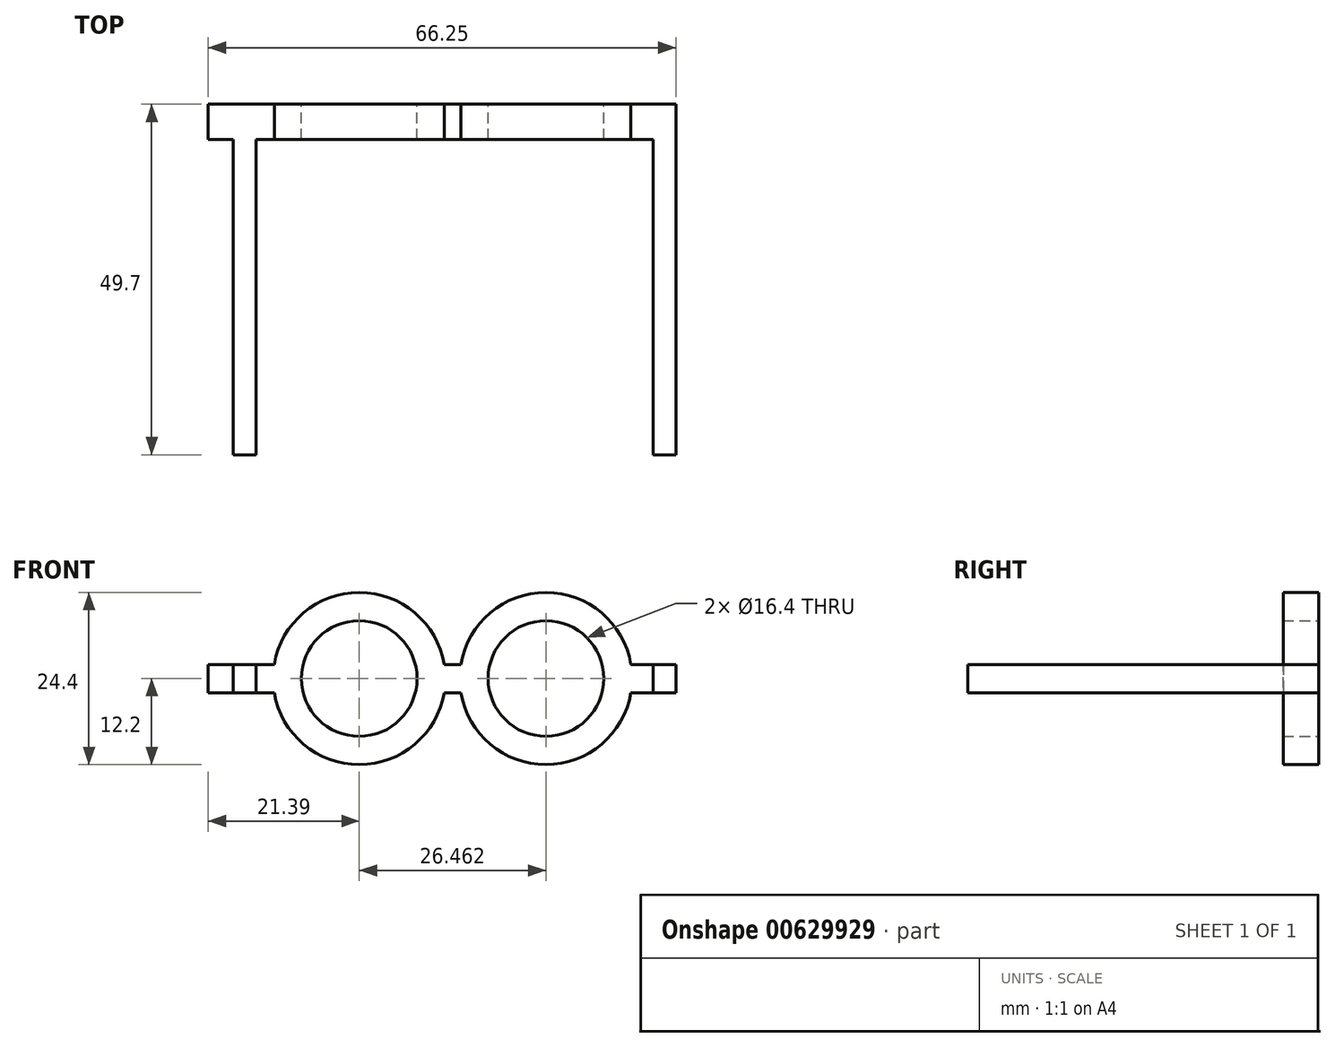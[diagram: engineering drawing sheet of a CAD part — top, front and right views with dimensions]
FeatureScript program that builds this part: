
annotation { "Feature Type Name" : "Feature", "Feature Type Description" : "" }
export const myFeature = defineFeature(function(context is Context, id is Id, definition is map)
    precondition{}
    {
        {
            var Q0;
            Q0=qCreatedBy(makeId("Front.planeOp"),FACE);
            var sketch = newSketch(context, id + "F0", { "sketchPlane" : qUnion([Q0])});
            skCircle(sketch, "E0", {"center": v(0, 0) * mm, "radius": 8.2 * mm});
            skArc(sketch, "E1.0", {"start": v(-12.03, -2) * mm, "mid": v(0, -12.2) * mm, "end": v(12.03, -2) * mm});
            skCircle(sketch, "E2", {"center": v(26.46, 0) * mm, "radius": 8.2 * mm});
            skArc(sketch, "E3.0", {"start": v(38.5, 2) * mm, "mid": v(26.46, 12.2) * mm, "end": v(14.43, 2) * mm});
            skPoint(sketch, "E4.middle", {"position": v(26.16, 0) * mm});
            skLineSegment(sketch, "E5.bottom", {"start": v(44.86, 2) * mm, "end": v(38.5, 2) * mm});
            skLineSegment(sketch, "E5.top", {"start": v(44.86, -2) * mm, "end": v(38.5, -2) * mm});
            skLineSegment(sketch, "E5.left", {"start": v(44.86, -2) * mm, "end": v(44.86, 2) * mm});
            skPoint(sketch, "E5.middle", {"position": v(35.66, 0) * mm});
            skPoint(sketch, "E6.middle", {"position": v(10.4, 0) * mm});
            skPoint(sketch, "E7.orphan", {"position": v(26.46, 2) * mm});
            skPoint(sketch, "E8.trimOffspring.end.orphan", {"position": v(26.46, -2) * mm});
            skLineSegment(sketch, "E9.bottom", {"start": v(-12.03, -2) * mm, "end": v(-21.4, -2) * mm});
            skLineSegment(sketch, "E9.top", {"start": v(-12.03, 2) * mm, "end": v(-21.4, 2) * mm});
            skLineSegment(sketch, "E9.right", {"start": v(-21.4, -2) * mm, "end": v(-21.4, 2) * mm});
            skPoint(sketch, "E9.middle", {"position": v(-10.7, 0) * mm});
            skPoint(sketch, "E10.orphan", {"position": v(0, 2) * mm});
            skPoint(sketch, "E11.orphan", {"position": v(0, -2) * mm});
            skLineSegment(sketch, "E12.bottom", {"start": v(14.43, -2) * mm, "end": v(12.03, -2) * mm});
            skLineSegment(sketch, "E12.top", {"start": v(14.43, 2) * mm, "end": v(12.03, 2) * mm});
            skPoint(sketch, "E12.middle", {"position": v(13.46, 0) * mm});
            skPoint(sketch, "E12.left.end.orphan", {"position": v(16.96, 2) * mm});
            skPoint(sketch, "E13.orphan", {"position": v(16.96, -2) * mm});
            skArc(sketch, "E14.trimOffspring", {"start": v(14.43, -2) * mm, "mid": v(26.46, -12.2) * mm, "end": v(38.5, -2) * mm});
            skArc(sketch, "E15.trimOffspring", {"start": v(12.03, 2) * mm, "mid": v(0, 12.2) * mm, "end": v(-12.03, 2) * mm});
            skPoint(sketch, "E16.orphan", {"position": v(9.96, 2) * mm});
            skPoint(sketch, "E17.orphan", {"position": v(9.96, -2) * mm});
            skSolve(sketch);
        }
        {
            var Q0;
            Q0=makeQuery(id+"F0.imprint","IMPRINT",FACE,{"disambiguationData":[TD([[makeQuery(id+"F0.imprint","IMPRINT",EDGE,{"derivedFrom":sQuery(id+"F0.wireOp",EDGE,"E0")}),-1.0]])]});
            extrude(context, id + "F1", {"entities" : qUnion([Q0]), "depth" : 5 * mm, "offsetDistance" : 25 * mm});
        }
        {
            var Q0;
            Q0=makeQuery(id+"F1.opExtrude","CAP_FACE",FACE,{"disambiguationData":[OSD([sQuery(id+"F0.wireOp",EDGE,"E0"),sQuery(id+"F0.wireOp",EDGE,"E1.0"),sQuery(id+"F0.wireOp",EDGE,"E2"),sQuery(id+"F0.wireOp",EDGE,"E3.0"),sQuery(id+"F0.wireOp",EDGE,"E5.bottom"),sQuery(id+"F0.wireOp",EDGE,"E5.top"),sQuery(id+"F0.wireOp",EDGE,"E5.left"),sQuery(id+"F0.wireOp",EDGE,"E9.bottom"),sQuery(id+"F0.wireOp",EDGE,"E9.top"),sQuery(id+"F0.wireOp",EDGE,"E9.right"),sQuery(id+"F0.wireOp",EDGE,"E12.bottom"),sQuery(id+"F0.wireOp",EDGE,"E12.top"),sQuery(id+"F0.wireOp",EDGE,"E14.trimOffspring"),sQuery(id+"F0.wireOp",EDGE,"E15.trimOffspring")])],"isStart":false});
            var sketch = newSketch(context, id + "F2", { "sketchPlane" : qUnion([Q0])});
            skLineSegment(sketch, "E18.bottom", {"start": v(-17.83, 2) * mm, "end": v(-14.64, 2) * mm});
            skLineSegment(sketch, "E18.top", {"start": v(-17.83, -2) * mm, "end": v(-14.64, -2) * mm});
            skLineSegment(sketch, "E18.left", {"start": v(-17.83, 2) * mm, "end": v(-17.83, -2) * mm});
            skLineSegment(sketch, "E18.right", {"start": v(-14.64, 2) * mm, "end": v(-14.64, -2) * mm});
            skLineSegment(sketch, "E19.bottom", {"start": v(41.68, 2) * mm, "end": v(44.86, 2) * mm});
            skLineSegment(sketch, "E19.top", {"start": v(41.68, -2) * mm, "end": v(44.86, -2) * mm});
            skLineSegment(sketch, "E19.left", {"start": v(41.68, 2) * mm, "end": v(41.68, -2) * mm});
            skLineSegment(sketch, "E19.right", {"start": v(44.86, 2) * mm, "end": v(44.86, -2) * mm});
            skSolve(sketch);
        }
        {
            var Q0;
            Q0=makeQuery(id+"F2.imprint","IMPRINT",FACE,{"disambiguationData":[TD([[makeQuery(id+"F2.imprint","IMPRINT",EDGE,{"derivedFrom":sQuery(id+"F2.wireOp",EDGE,"E18.bottom")}),1.0]])]});
            var Q1;
            Q1=makeQuery(id+"F2.imprint","IMPRINT",FACE,{"disambiguationData":[TD([[makeQuery(id+"F2.imprint","IMPRINT",EDGE,{"derivedFrom":sQuery(id+"F2.wireOp",EDGE,"E19.bottom")}),1.0]])]});
            extrude(context, id + "F3", {"entities" : qUnion([Q0, Q1]), "operationType" : NewBodyOperationType.ADD, "depth" : 44.7 * mm, "offsetDistance" : 25 * mm});
        }
    });
